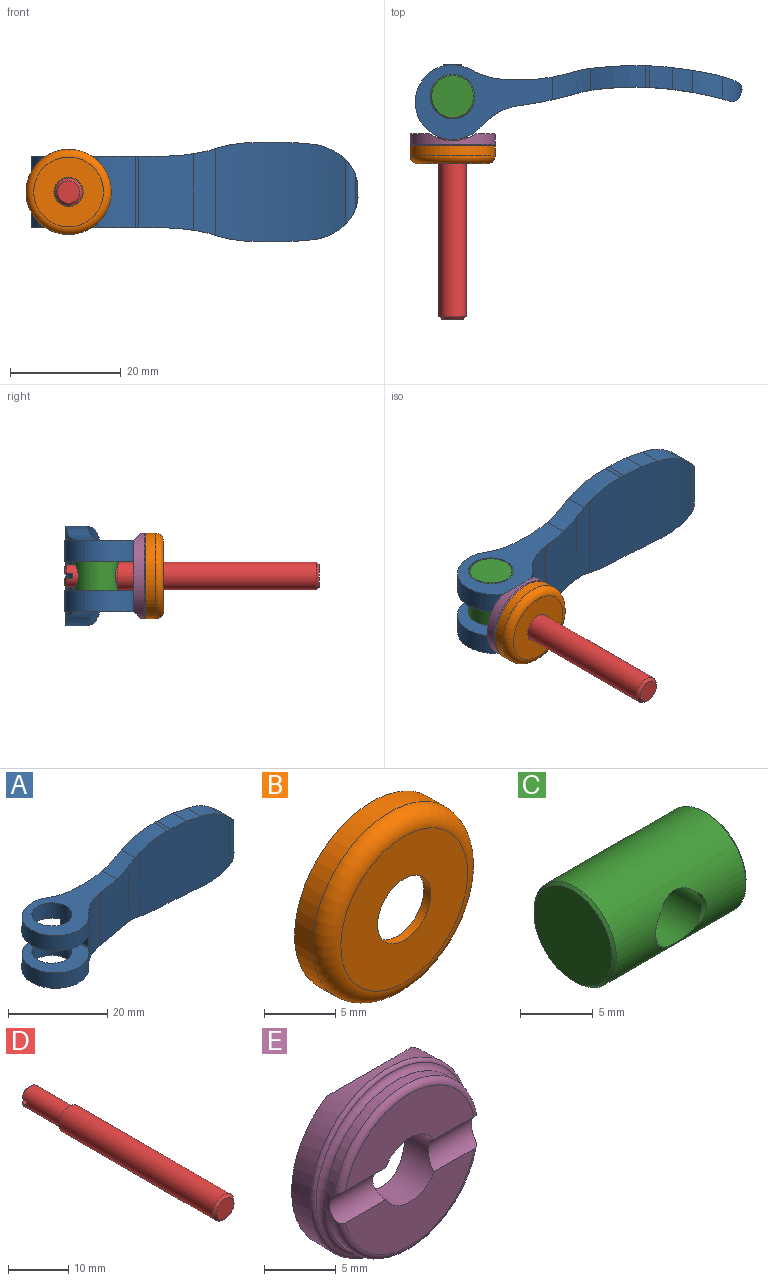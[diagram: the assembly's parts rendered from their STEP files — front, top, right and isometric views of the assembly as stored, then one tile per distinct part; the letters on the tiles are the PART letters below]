
ASSEMBLY  parts=5 mates=4
PART A: 40 faces, bbox 59.1x13.6x18.1 mm
  f0: cylinder r=35mm len=13.55mm, axis (0,0,-1), area 164mm2, adj f1,f7,f23,f24,f30,f31
  f1: cylinder r=20mm len=15.78mm, axis (0,0,-1), area 71mm2, adj f0,f8,f24,f25,f31,f32
  f2: plane 6.11x0.8mm, normal (0.92,-0.39,0), area 3.8mm2, adj f10,f11,f19,f28
  f3: cylinder r=24mm len=15.78mm, axis (0,0,-1), area 58.4mm2, adj f4,f12,f24,f25,f31,f32
  f4: cylinder r=74mm len=13.82mm, axis (0,0,-1), area 133.1mm2, adj f3,f13,f23,f24,f30,f31
  f5: cylinder r=6.8mm len=3.8mm, axis (0,0,-1), area 5.1mm2, adj f6,f14,f30,f33
  f6: cylinder r=6.75mm len=13.5mm, axis (0,0,-1), area 111.3mm2, adj f5,f7,f30,f33
  f7: cylinder r=13.3mm len=13mm, axis (0,0,-1), area 64.2mm2, adj f0,f6,f16,f23,f30,f33,f34,f35
  f8: cylinder r=64mm len=21.5mm, axis (0,0,-1), area 375.5mm2, adj f1,f9,f17,f18,f20,f21,f22,f25
  f9: cylinder r=20mm len=14.7mm, axis (0,0,-1), area 42.4mm2, adj f8,f10,f19,f21,f27,f28
  f10: cylinder r=1.5mm len=8.46mm, axis (0,0,-1), area 10.9mm2, adj f2,f9,f19,f28
  f11: cylinder r=1.5mm len=11.81mm, axis (0,0,-1), area 20.4mm2, adj f2,f12,f19,f28
  f12: cylinder r=60mm len=23.5mm, axis (0,0,-1), area 403.6mm2, adj f3,f11,f17,f18,f19,f20,f21,f22
  f13: cylinder r=74mm len=13mm, axis (0,0,-1), area 7.8mm2, adj f4,f14,f23,f30
  f14: cylinder r=10.8mm len=13mm, axis (0,0,-1), area 97mm2, adj f5,f13,f15,f23,f30,f33,f34,f35
  f15: cylinder r=6.8mm len=3.8mm, axis (0,0,-1), area 5.1mm2, adj f14,f16,f23,f37
  f16: cylinder r=6.75mm len=13.5mm, axis (0,0,-1), area 111.3mm2, adj f7,f15,f23,f37
  f17: plane 4.26x4.2mm, normal (0,0,1), area 16.5mm2, adj f8,f12,f26,f29
  f18: plane 4.26x4.2mm, normal (0,0,-1), area 16.5mm2, adj f8,f12,f20,f22
  f19: cylinder r=7.5mm len=5.93mm, axis (0,-1,0), area 21.4mm2, adj f2,f9,f10,f11,f12,f21
  f20: cylinder r=39mm len=4.48mm, axis (0,-1,0), area 14.4mm2, adj f8,f12,f18,f21
  f21: cylinder r=10mm len=5.3mm, axis (0,-1,0), area 22.9mm2, adj f8,f9,f12,f19,f20
  f22: cylinder r=70mm len=3.94mm, axis (0,-1,0), area 3mm2, adj f8,f12,f18,f25
  f23: plane 24.75x13.5mm, normal (0,0,-1), area 151mm2, adj f0,f4,f7,f13,f14,f15,f16,f24
  f24: cylinder r=31mm len=7mm, axis (0,-1,0), area 28.7mm2, adj f0,f1,f3,f4,f23,f25
  f25: cylinder r=27mm len=9.83mm, axis (0,-1,0), area 39.2mm2, adj f1,f3,f8,f12,f22,f24
  f26: cylinder r=39mm len=4.48mm, axis (0,-1,0), area 14.4mm2, adj f8,f12,f17,f27
  f27: cylinder r=10mm len=5.3mm, axis (0,-1,0), area 22.9mm2, adj f8,f9,f12,f26,f28
  f28: cylinder r=7.5mm len=5.93mm, axis (0,-1,0), area 21.4mm2, adj f2,f9,f10,f11,f12,f27
  f29: cylinder r=70mm len=3.94mm, axis (0,-1,0), area 3mm2, adj f8,f12,f17,f32
  f30: plane 24.75x13.5mm, normal (0,0,1), area 151mm2, adj f0,f4,f5,f6,f7,f13,f14,f31
  f31: cylinder r=31mm len=7mm, axis (0,-1,0), area 28.7mm2, adj f0,f1,f3,f4,f30,f32
  f32: cylinder r=27mm len=9.83mm, axis (0,-1,0), area 39.2mm2, adj f1,f3,f8,f12,f29,f31
  f33: plane 13.5x12.75mm, normal (0,0,-1), area 89.9mm2, adj f5,f6,f7,f14,f34,f39
  f34: cylinder r=0.2mm len=8.22mm, axis (0,-1,0), area 2.5mm2, adj f7,f14,f33,f35
  f35: plane 7.97x5mm, normal (-1,0,0), area 39.9mm2, adj f7,f14,f34,f36
  f36: cylinder r=0.2mm len=8.22mm, axis (0,-1,0), area 2.5mm2, adj f7,f14,f35,f37
  f37: plane 13.5x12.75mm, normal (0,0,1), area 89.9mm2, adj f7,f14,f15,f16,f36,f38
  f38: cylinder r=4.05mm len=8.1mm, axis (0,0,-1), area 96.7mm2, adj f23,f37
  f39: cylinder r=4.05mm len=8.1mm, axis (0,0,-1), area 96.7mm2, adj f30,f33
PART B: 8 faces, bbox 16.7x3.2x16.7 mm
  f0: plane 12.6x12.6mm, normal (0,1,0), area 102.6mm2, adj f1,f7
  f1: torus R=6.3mm, axis (0,-1,0), area 46.6mm2, adj f0,f2
  f2: cylinder r=7mm len=14mm, axis (0,-1,0), area 79.2mm2, adj f1,f3
  f3: plane 15.4x15.4mm, normal (0,1,0), area 32.3mm2, adj f2,f4
  f4: cylinder r=7.7mm len=15.4mm, axis (0,-1,0), area 87.1mm2, adj f3,f5
  f5: torus R=6.3mm, axis (0,-1,0), area 99.4mm2, adj f4,f6
  f6: plane 12.6x12.6mm, normal (0,-1,0), area 102.6mm2, adj f5,f7
  f7: cylinder r=2.65mm len=5.3mm, axis (0,-1,0), area 11.7mm2, adj f0,f6
PART C: 10 faces, bbox 13x8x8 mm
  f0: cylinder r=4mm len=12.58mm, axis (1,0,0), area 281.2mm2, adj f2,f3,f5,f6,f7,f8,f9
  f1: plane 7.58x7.58mm, normal (-1,0,0), area 45.1mm2, adj f2
  f2: cone r=3.79mm half-angle=45deg, axis (1,0,0), area 7.3mm2, adj f0,f1
  f3: cone r=4mm half-angle=45deg, axis (-1,0,0), area 7.3mm2, adj f0,f4
  f4: plane 7.58x7.58mm, normal (1,0,0), area 45.1mm2, adj f3
  f5: cone r=2.5mm half-angle=45deg, axis (0,1,0), area 0.8mm2, adj f0,f7
  f6: cone r=2.5mm half-angle=45deg, axis (0,1,0), area 0.8mm2, adj f0,f7
  f7: cylinder r=2.23mm len=7.46mm, axis (0,-1,0), area 100.6mm2, adj f0,f5,f6,f8,f9
  f8: cone r=2.23mm half-angle=45deg, axis (0,-1,0), area 0.8mm2, adj f0,f7
  f9: cone r=2.23mm half-angle=45deg, axis (0,-1,0), area 0.8mm2, adj f0,f7
PART D: 12 faces, bbox 5x46x5 mm
  f0: plane 3.29x1.29mm, normal (0,1,0), area 3.2mm2, adj f1,f11
  f1: cone r=1.69mm half-angle=45deg, axis (0,-1,0), area 2.2mm2, adj f0,f2,f11
  f2: cylinder r=2mm len=9.19mm, axis (0,-1,0), area 113.7mm2, adj f1,f4,f5,f9,f10,f11
  f3: plane 3.29x1.29mm, normal (0,1,0), area 3.2mm2, adj f4,f10
  f4: cone r=1.69mm half-angle=45deg, axis (0,-1,0), area 2.2mm2, adj f2,f3,f10
  f5: plane 5x5mm, normal (0,1,0), area 7.1mm2, adj f2,f6
  f6: cylinder r=2.5mm len=36.01mm, axis (0,-1,0), area 565.6mm2, adj f5,f7
  f7: cone r=2.5mm half-angle=45deg, axis (0,1,0), area 9.8mm2, adj f6,f8
  f8: plane 4.02x4.02mm, normal (0,-1,0), area 12.7mm2, adj f7
  f9: cylinder r=31.5mm len=3.92mm, axis (0,0,-1), area 3.1mm2, adj f2,f10,f11
  f10: plane 3.93x1.51mm, normal (0,0,-1), area 5.7mm2, adj f2,f3,f4,f9
  f11: plane 3.93x1.51mm, normal (0,0,1), area 5.7mm2, adj f0,f1,f2,f9
PART E: 14 faces, bbox 16.7x4x16.7 mm
  f0: cylinder r=7mm len=14mm, axis (0,-1,0), area 34.4mm2, adj f1,f2,f11,f12,f13
  f1: torus R=6.5mm, axis (0,-1,0), area 14.8mm2, adj f0,f4,f12,f13
  f2: torus R=6.5mm, axis (0,-1,0), area 14.8mm2, adj f0,f3,f12,f13
  f3: plane 12.71x5.13mm, normal (0,-1,0), area 44mm2, adj f2,f5,f12,f13
  f4: plane 12.71x5.13mm, normal (0,-1,0), area 44mm2, adj f1,f5,f12,f13
  f5: cylinder r=2.75mm len=5.5mm, axis (0,-1,0), area 47.4mm2, adj f3,f4,f6,f12,f13
  f6: cylinder r=7.5mm len=15.37mm, axis (0,0,-1), area 105.8mm2, adj f5,f7,f8,f9
  f7: plane 12.79x3.44mm, normal (0,1,0), area 31mm2, adj f6,f9
  f8: plane 12.79x3.44mm, normal (0,1,0), area 31mm2, adj f6,f9
  f9: cone r=7.66mm half-angle=1deg, axis (0,-1,0), area 76mm2, adj f6,f7,f8,f10
  f10: torus R=7.39mm, axis (0,-1,0), area 20.9mm2, adj f9,f11
  f11: torus R=7.5mm, axis (0,-1,0), area 32.3mm2, adj f0,f10
  f12: cylinder r=1.5mm len=4.62mm, axis (-1,0,0), area 15mm2, adj f0,f1,f2,f3,f4,f5
  f13: cylinder r=1.5mm len=4.62mm, axis (-1,0,0), area 15mm2, adj f0,f1,f2,f3,f4,f5
PLACE A at identity
PLACE B t=(0,-12.09,0)mm
PLACE C rot(axis=(0,1,0),90deg) t=(0,0,0)mm fixed
PLACE D t=(0,-40.23,0)mm
PLACE E t=(0,-10.69,0)mm
MATE revolute C.f0 <-> A.f38  axis (0,0,-1) through (0,0,-6.5)mm
MATE fastened E.f0 <-> B.f1  axis (0,-1,0) through (0,-8.89,0)mm
MATE slider D.f1 <-> B.f1  axis (0,-1,0) through (0,-21.73,0)mm
MATE revolute D.f1 <-> C.f5  axis (0,-1,0) through (0,-3.73,0)mm
